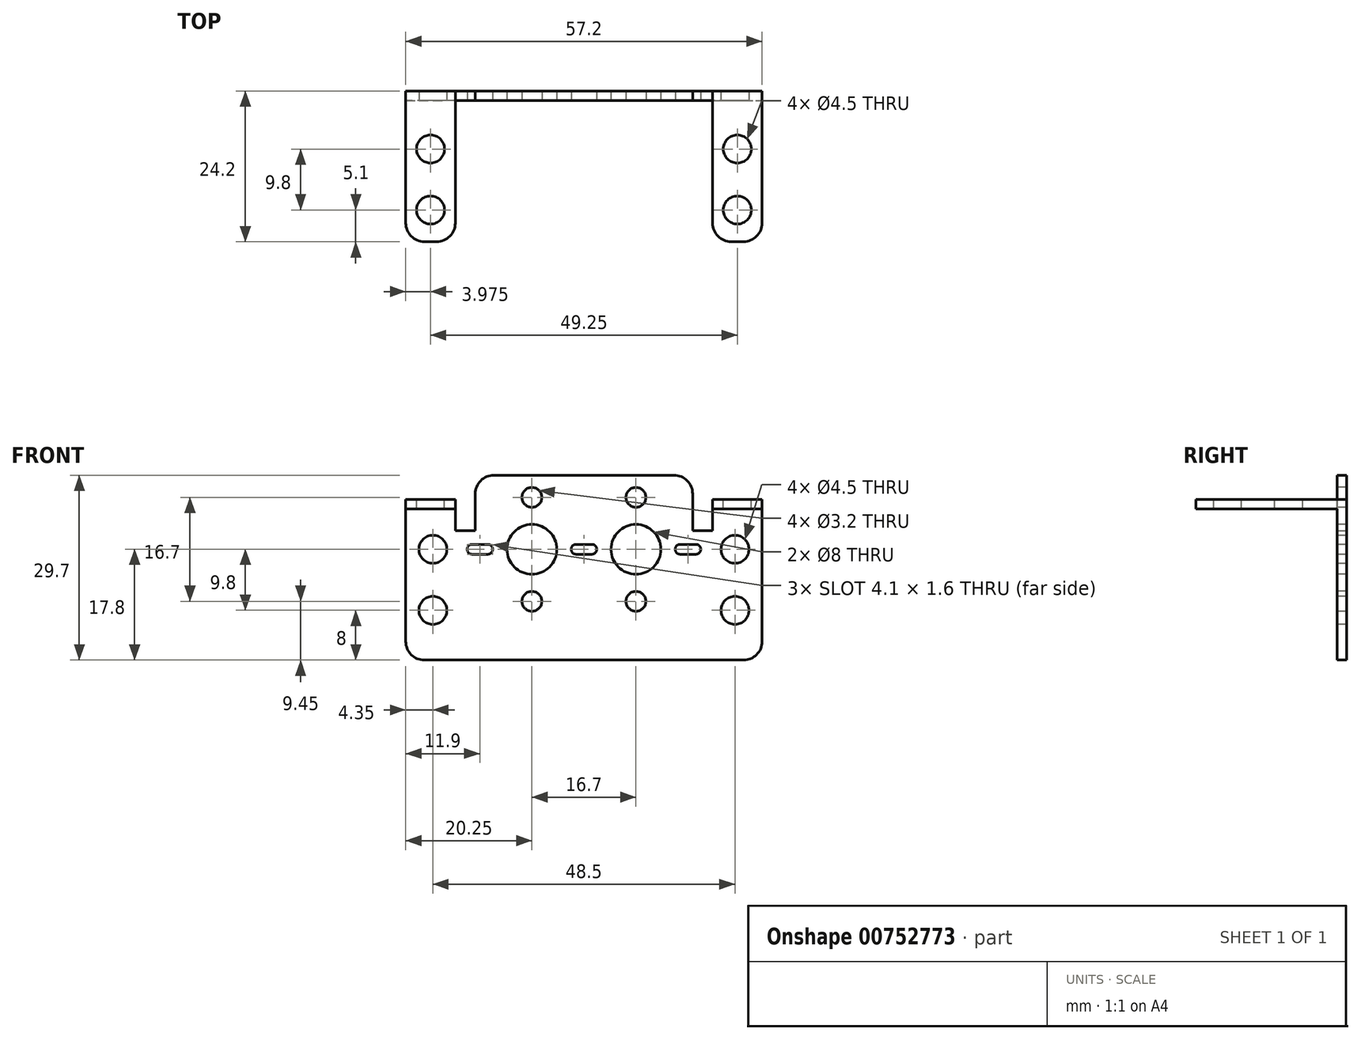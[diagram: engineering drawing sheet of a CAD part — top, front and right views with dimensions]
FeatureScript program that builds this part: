
annotation { "Feature Type Name" : "Feature", "Feature Type Description" : "" }
export const myFeature = defineFeature(function(context is Context, id is Id, definition is map)
    precondition{}
    {
        {
            var Q0;
            Q0=qCreatedBy(makeId("Front.planeOp"),FACE);
            var sketch = newSketch(context, id + "F0", { "sketchPlane" : qUnion([Q0])});
            skLineSegment(sketch, "E0.bottom", {"start": v(25.6, -14.85) * mm, "end": v(-25.6, -14.85) * mm});
            skLineSegment(sketch, "E0.left", {"start": v(28.6, -11.85) * mm, "end": v(28.6, 10.95) * mm});
            skLineSegment(sketch, "E0.right", {"start": v(-28.6, -11.85) * mm, "end": v(-28.6, 10.95) * mm});
            skPoint(sketch, "E0.middle", {"position": v(0, 0) * mm});
            skLineSegment(sketch, "E1", {"start": v(-14.45, 14.85) * mm, "end": v(14.45, 14.85) * mm});
            skLineSegment(sketch, "E2.0", {"start": v(-28.6, 10.95) * mm, "end": v(-20.65, 10.95) * mm});
            skLineSegment(sketch, "E3.0", {"start": v(-20.65, 5.95) * mm, "end": v(-17.45, 5.95) * mm});
            skLineSegment(sketch, "E4.0", {"start": v(-17.45, 11.85) * mm, "end": v(-17.45, 5.95) * mm});
            skLineSegment(sketch, "E5.0", {"start": v(-20.65, 10.95) * mm, "end": v(-20.65, 5.95) * mm});
            skPoint(sketch, "E6.visualSharp", {"position": v(-28.6, -14.85) * mm});
            skArc(sketch, "E6.filletArc", {"start": v(-28.6, -11.85) * mm, "mid": v(-27.72, -13.97) * mm, "end": v(-25.6, -14.85) * mm});
            skPoint(sketch, "E7.visualSharp", {"position": v(28.6, -14.85) * mm});
            skArc(sketch, "E7.filletArc", {"start": v(25.6, -14.85) * mm, "mid": v(27.72, -13.97) * mm, "end": v(28.6, -11.85) * mm});
            skArc(sketch, "E8.filletArc", {"start": v(-14.45, 14.85) * mm, "mid": v(-16.57, 13.97) * mm, "end": v(-17.45, 11.85) * mm});
            skLineSegment(sketch, "E9.MirrorCS", {"start": v(17.45, 11.85) * mm, "end": v(17.45, 5.95) * mm});
            skLineSegment(sketch, "E10.MirrorCS", {"start": v(20.65, 10.95) * mm, "end": v(20.65, 5.95) * mm});
            skLineSegment(sketch, "E11.MirrorCS", {"start": v(20.65, 5.95) * mm, "end": v(17.45, 5.95) * mm});
            skLineSegment(sketch, "E12.MirrorCS", {"start": v(28.6, 10.95) * mm, "end": v(20.65, 10.95) * mm});
            skArc(sketch, "E13.MirrorCS", {"start": v(14.45, 14.85) * mm, "mid": v(16.57, 13.97) * mm, "end": v(17.45, 11.85) * mm});
            skSolve(sketch);
        }
        {
            var Q0;
            Q0 = qSketchRegion(id + "F0", true);
            extrude(context, id + "F1", {"entities" : qUnion([Q0]), "depth" : 1.5 * mm, "offsetDistance" : 25 * mm});
        }
        {
            var Q0;
            Q0=makeQuery(id+"F1.opExtrude","CAP_FACE",FACE,{"disambiguationData":[OSD([sQuery(id+"F0.wireOp",EDGE,"E0.bottom"),sQuery(id+"F0.wireOp",EDGE,"E0.left"),sQuery(id+"F0.wireOp",EDGE,"E0.right"),sQuery(id+"F0.wireOp",EDGE,"E1"),sQuery(id+"F0.wireOp",EDGE,"E2.0"),sQuery(id+"F0.wireOp",EDGE,"E3.0"),sQuery(id+"F0.wireOp",EDGE,"E4.0"),sQuery(id+"F0.wireOp",EDGE,"E5.0"),sQuery(id+"F0.wireOp",EDGE,"E6.filletArc"),sQuery(id+"F0.wireOp",EDGE,"E7.filletArc"),sQuery(id+"F0.wireOp",EDGE,"E8.filletArc"),sQuery(id+"F0.wireOp",EDGE,"E9.MirrorCS"),sQuery(id+"F0.wireOp",EDGE,"E10.MirrorCS"),sQuery(id+"F0.wireOp",EDGE,"E11.MirrorCS"),sQuery(id+"F0.wireOp",EDGE,"E12.MirrorCS"),sQuery(id+"F0.wireOp",EDGE,"E13.MirrorCS")])],"isStart":false});
            var sketch = newSketch(context, id + "F2", { "sketchPlane" : qUnion([Q0])});
            skLineSegment(sketch, "E14.bottom", {"start": v(-20.65, 10.95) * mm, "end": v(-28.6, 10.95) * mm});
            skLineSegment(sketch, "E14.top", {"start": v(-20.65, 9.45) * mm, "end": v(-28.6, 9.45) * mm});
            skLineSegment(sketch, "E14.left", {"start": v(-20.65, 10.95) * mm, "end": v(-20.65, 9.45) * mm});
            skLineSegment(sketch, "E14.right", {"start": v(-28.6, 10.95) * mm, "end": v(-28.6, 9.45) * mm});
            skLineSegment(sketch, "E15.bottom", {"start": v(20.65, 10.95) * mm, "end": v(28.6, 10.95) * mm});
            skLineSegment(sketch, "E15.top", {"start": v(20.65, 9.45) * mm, "end": v(28.6, 9.45) * mm});
            skLineSegment(sketch, "E15.left", {"start": v(20.65, 10.95) * mm, "end": v(20.65, 9.45) * mm});
            skLineSegment(sketch, "E15.right", {"start": v(28.6, 10.95) * mm, "end": v(28.6, 9.45) * mm});
            skSolve(sketch);
        }
        {
            var Q0;
            Q0 = qSketchRegion(id + "F2", true);
            extrude(context, id + "F3", {"entities" : qUnion([Q0]), "operationType" : NewBodyOperationType.ADD, "depth" : 22.7 * mm, "offsetDistance" : 25 * mm});
        }
        {
            var Q0;
            Q0=makeQuery(id+"F3.opExtrude","CAP_EDGE",EDGE,{"disambiguationData":[OSD([sQuery(id+"F2.wireOp",EDGE,"E14.right")])],"isStart":false});
            var Q1;
            Q1=makeQuery(id+"F3.opExtrude","CAP_EDGE",EDGE,{"disambiguationData":[OSD([sQuery(id+"F2.wireOp",EDGE,"E14.left")])],"isStart":false});
            var Q2;
            Q2=makeQuery(id+"F3.opExtrude","CAP_EDGE",EDGE,{"disambiguationData":[OSD([sQuery(id+"F2.wireOp",EDGE,"E15.left")])],"isStart":false});
            var Q3;
            Q3=makeQuery(id+"F3.opExtrude","CAP_EDGE",EDGE,{"disambiguationData":[OSD([sQuery(id+"F2.wireOp",EDGE,"E15.right")])],"isStart":false});
            fillet(context, id + "F4", {"entities" : qUnion([Q0, Q1, Q2, Q3]), "radius" : 3 * mm, "tangentPropagation" : true, "allowEdgeOverflow" : false});
        }
        {
            var Q0;
            Q0=makeQuery(id+"F3.boolean.opBoolean","MERGE",FACE,{"derivedFrom":[makeQuery(id+"F1.opExtrude","SWEPT_FACE",FACE,{"disambiguationData":[OSD([sQuery(id+"F0.wireOp",EDGE,"E12.MirrorCS")])]}),makeQuery(id+"F3.opExtrude","SWEPT_FACE",FACE,{"disambiguationData":[OSD([sQuery(id+"F2.wireOp",EDGE,"E15.bottom")])]})]});
            var sketch = newSketch(context, id + "F5", { "sketchPlane" : qUnion([Q0])});
            skLineSegment(sketch, "E16", {"start": v(28.6, 0) * mm, "end": v(20.65, 0) * mm});
            skCircle(sketch, "E17", {"center": v(24.62, -9.3) * mm, "radius": 2.25 * mm});
            skCircle(sketch, "E18", {"center": v(24.62, -19.1) * mm, "radius": 2.25 * mm});
            skCircle(sketch, "E19.MirrorC", {"center": v(-24.62, -9.3) * mm, "radius": 2.25 * mm});
            skCircle(sketch, "E20.MirrorC", {"center": v(-24.62, -19.1) * mm, "radius": 2.25 * mm});
            skSolve(sketch);
        }
        {
            var Q0;
            Q0 = qSketchRegion(id + "F5", true);
            extrude(context, id + "F6", {"entities" : qUnion([Q0]), "operationType" : NewBodyOperationType.REMOVE, "oppositeDirection" : true, "depth" : 1.5 * mm, "offsetDistance" : 25 * mm});
        }
        {
            var Q0;
            Q0=makeQuery(id+"F1.opExtrude","CAP_FACE",FACE,{"disambiguationData":[OSD([sQuery(id+"F0.wireOp",EDGE,"E0.bottom"),sQuery(id+"F0.wireOp",EDGE,"E0.left"),sQuery(id+"F0.wireOp",EDGE,"E0.right"),sQuery(id+"F0.wireOp",EDGE,"E1"),sQuery(id+"F0.wireOp",EDGE,"E2.0"),sQuery(id+"F0.wireOp",EDGE,"E3.0"),sQuery(id+"F0.wireOp",EDGE,"E4.0"),sQuery(id+"F0.wireOp",EDGE,"E5.0"),sQuery(id+"F0.wireOp",EDGE,"E6.filletArc"),sQuery(id+"F0.wireOp",EDGE,"E7.filletArc"),sQuery(id+"F0.wireOp",EDGE,"E8.filletArc"),sQuery(id+"F0.wireOp",EDGE,"E9.MirrorCS"),sQuery(id+"F0.wireOp",EDGE,"E10.MirrorCS"),sQuery(id+"F0.wireOp",EDGE,"E11.MirrorCS"),sQuery(id+"F0.wireOp",EDGE,"E12.MirrorCS"),sQuery(id+"F0.wireOp",EDGE,"E13.MirrorCS")])],"isStart":false});
            var sketch = newSketch(context, id + "F7", { "sketchPlane" : qUnion([Q0])});
            skLineSegment(sketch, "E21.0", {"start": v(-28.6, 2.95) * mm, "end": v(-26.5, 2.95) * mm});
            skCircle(sketch, "E22", {"center": v(-24.25, 2.95) * mm, "radius": 2.25 * mm});
            skArc(sketch, "E23", {"start": v(-17.95, 3.75) * mm, "mid": v(-18.75, 2.95) * mm, "end": v(-17.95, 2.15) * mm});
            skArc(sketch, "E24", {"start": v(-15.45, 2.15) * mm, "mid": v(-14.65, 2.95) * mm, "end": v(-15.45, 3.75) * mm});
            skLineSegment(sketch, "E25", {"start": v(-15.45, 3.75) * mm, "end": v(-17.95, 3.75) * mm});
            skLineSegment(sketch, "E26", {"start": v(-17.95, 2.15) * mm, "end": v(-15.45, 2.15) * mm});
            skCircle(sketch, "E27", {"center": v(-8.35, 2.95) * mm, "radius": 4 * mm});
            skCircle(sketch, "E28", {"center": v(-8.35, 11.3) * mm, "radius": 1.6 * mm});
            skCircle(sketch, "E29.MirrorC", {"center": v(-8.35, -5.4) * mm, "radius": 1.6 * mm});
            skCircle(sketch, "E30.MirrorC", {"center": v(8.35, 2.95) * mm, "radius": 4 * mm});
            skCircle(sketch, "E31.MirrorC", {"center": v(8.35, 11.3) * mm, "radius": 1.6 * mm});
            skCircle(sketch, "E32.MirrorC", {"center": v(8.35, -5.4) * mm, "radius": 1.6 * mm});
            skArc(sketch, "E33.MirrorCS", {"start": v(15.45, 2.15) * mm, "mid": v(14.65, 2.95) * mm, "end": v(15.45, 3.75) * mm});
            skCircle(sketch, "E34.MirrorC", {"center": v(24.25, 2.95) * mm, "radius": 2.25 * mm});
            skLineSegment(sketch, "E35.MirrorCS", {"start": v(17.95, 2.15) * mm, "end": v(15.45, 2.15) * mm});
            skLineSegment(sketch, "E36.MirrorCS", {"start": v(15.45, 3.75) * mm, "end": v(17.95, 3.75) * mm});
            skArc(sketch, "E37.MirrorCS", {"start": v(17.95, 3.75) * mm, "mid": v(18.75, 2.95) * mm, "end": v(17.95, 2.15) * mm});
            skArc(sketch, "E38.MirrorCS", {"start": v(-1.25, 2.15) * mm, "mid": v(-2.05, 2.95) * mm, "end": v(-1.25, 3.75) * mm});
            skLineSegment(sketch, "E39.MirrorCS", {"start": v(1.25, 2.15) * mm, "end": v(-1.25, 2.15) * mm});
            skLineSegment(sketch, "E40.MirrorCS", {"start": v(-1.25, 3.75) * mm, "end": v(1.25, 3.75) * mm});
            skArc(sketch, "E41.MirrorCS", {"start": v(1.25, 3.75) * mm, "mid": v(2.05, 2.95) * mm, "end": v(1.25, 2.15) * mm});
            skCircle(sketch, "E42", {"center": v(-24.25, -6.85) * mm, "radius": 2.25 * mm});
            skCircle(sketch, "E43.MirrorC", {"center": v(24.25, -6.85) * mm, "radius": 2.25 * mm});
            skSolve(sketch);
        }
        {
            var Q0;
            Q0 = qSketchRegion(id + "F7", true);
            extrude(context, id + "F8", {"entities" : qUnion([Q0]), "operationType" : NewBodyOperationType.REMOVE, "oppositeDirection" : true, "depth" : 1.6 * mm, "offsetDistance" : 25 * mm});
        }
    });
